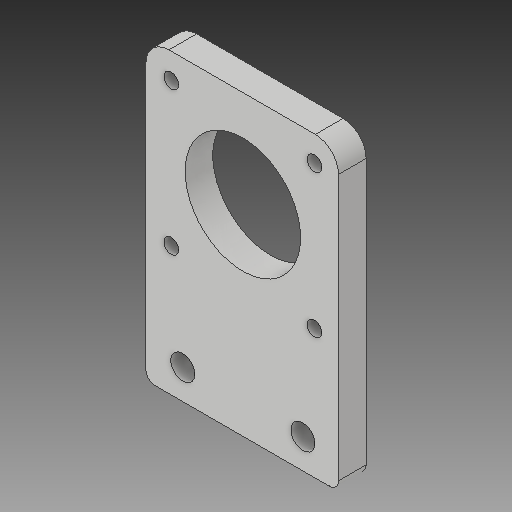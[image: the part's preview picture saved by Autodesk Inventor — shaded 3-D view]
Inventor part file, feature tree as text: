
AUTODESK INVENTOR PART (.ipt)
format: ipt  version: 2018 (Build 220112000, 112)  size: 150,528 bytes
history: native  units: mm
features: sketch x4, other x3
ambient origin geometry x8: Origin, YZ Plane, XZ Plane, XY Plane, X Axis, Y Axis, Z Axis, Center Point
bodies: Solid1 (feature_tree)
feature tree (7):
  other  "Z Motor Mount LC.ipt"
  other  "Solid1::Z Motor Mount LC.ipt"
  other  "TaggingFeature1"
  sketch  "Sketch1"  dims[d0=10.0mm]
  sketch  "Sketch2"
  sketch  "Sketch3"
  sketch  "Sketch4"
